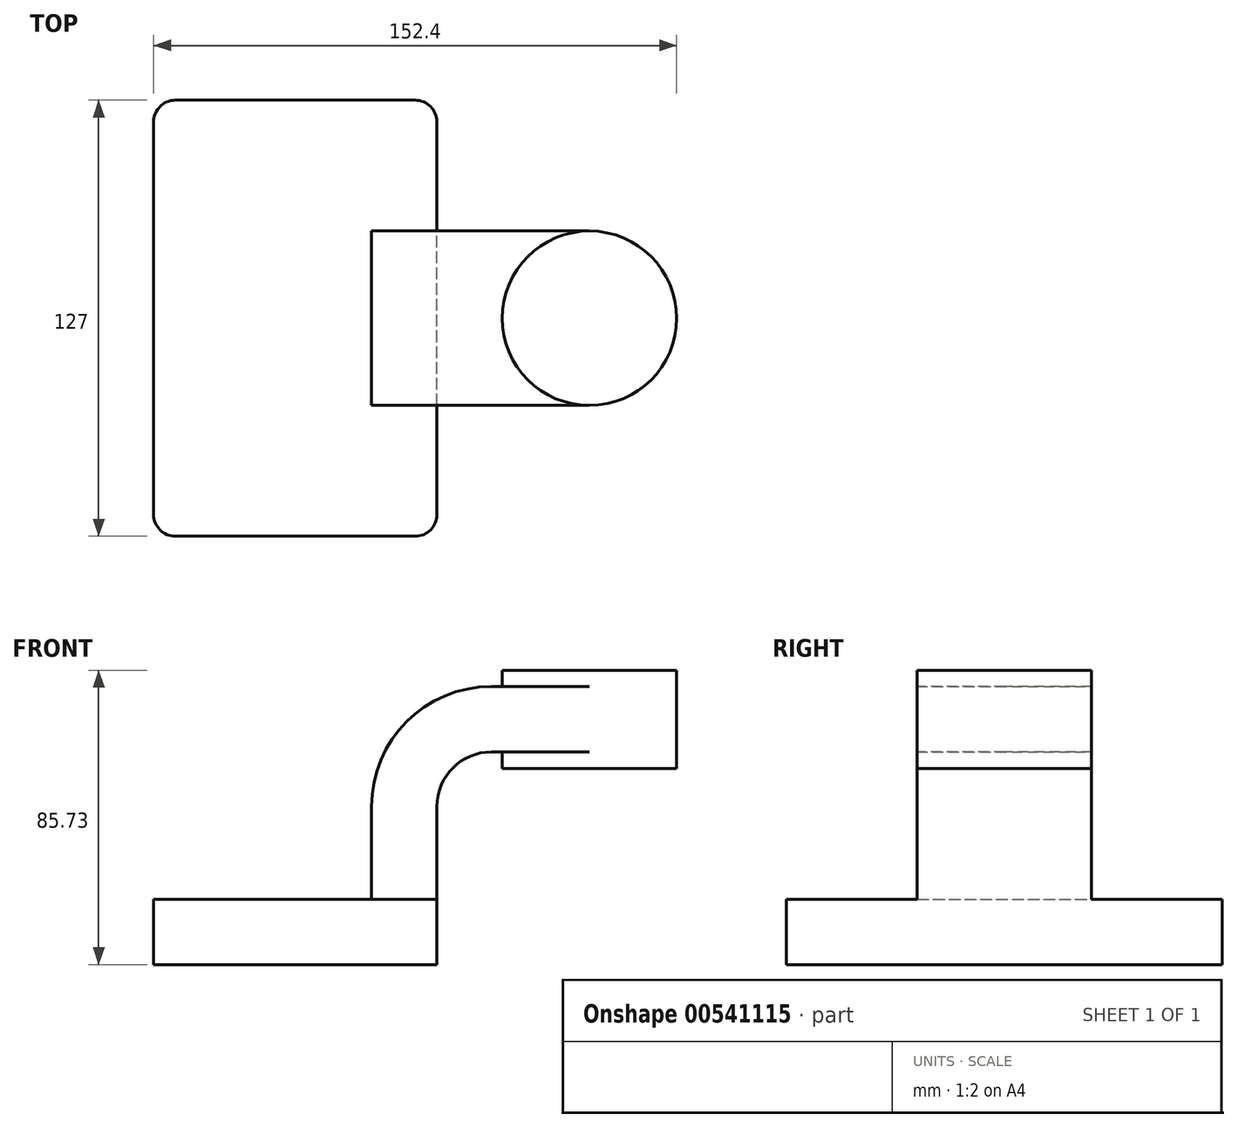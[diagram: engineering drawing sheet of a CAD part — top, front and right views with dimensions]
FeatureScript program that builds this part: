
annotation { "Feature Type Name" : "Feature", "Feature Type Description" : "" }
export const myFeature = defineFeature(function(context is Context, id is Id, definition is map)
    precondition{}
    {
        {
            var Q0;
            Q0=qCreatedBy(makeId("Front.planeOp"),FACE);
            var sketch = newSketch(context, id + "F0", { "sketchPlane" : qUnion([Q0])});
            skLineSegment(sketch, "E0.bottom", {"start": v(41.28, -9.52) * mm, "end": v(-41.27, -9.53) * mm});
            skLineSegment(sketch, "E0.top", {"start": v(41.27, 9.53) * mm, "end": v(-41.28, 9.53) * mm});
            skLineSegment(sketch, "E0.left", {"start": v(41.28, -9.52) * mm, "end": v(41.28, 9.53) * mm});
            skLineSegment(sketch, "E0.right", {"start": v(-41.27, -9.52) * mm, "end": v(-41.28, 9.53) * mm});
            skPoint(sketch, "E0.middle", {"position": v(0, 0) * mm});
            skLineSegment(sketch, "E1.bottom", {"start": v(111.12, 47.63) * mm, "end": v(60.33, 47.62) * mm});
            skLineSegment(sketch, "E1.top", {"start": v(111.12, 76.2) * mm, "end": v(60.33, 76.2) * mm});
            skLineSegment(sketch, "E1.left", {"start": v(111.12, 47.62) * mm, "end": v(111.12, 76.2) * mm});
            skLineSegment(sketch, "E1.right", {"start": v(60.33, 47.62) * mm, "end": v(60.33, 76.2) * mm});
            skPoint(sketch, "E1.middle", {"position": v(85.72, 61.91) * mm});
            skLineSegment(sketch, "E2", {"start": v(41.27, 9.53) * mm, "end": v(41.27, 36.53) * mm});
            skArc(sketch, "E3", {"start": v(41.27, 36.53) * mm, "mid": v(45.92, 47.75) * mm, "end": v(57.15, 52.4) * mm});
            skLineSegment(sketch, "E4", {"start": v(57.15, 52.4) * mm, "end": v(85.72, 52.4) * mm});
            skLineSegment(sketch, "E5.0", {"start": v(57.15, 71.45) * mm, "end": v(85.72, 71.45) * mm});
            skArc(sketch, "E5.1", {"start": v(22.23, 36.53) * mm, "mid": v(32.45, 61.22) * mm, "end": v(57.15, 71.45) * mm});
            skLineSegment(sketch, "E5.2", {"start": v(22.22, 9.53) * mm, "end": v(22.22, 36.53) * mm});
            skLineSegment(sketch, "E6", {"start": v(85.72, 47.62) * mm, "end": v(85.72, 76.2) * mm});
            skFitSpline(sketch, "E7", {"points": [v(-41.28, 9.53) * mm, v(57.15, 71.45) * mm], "startDerivative": vector(106.2, 48.35) * mm, "endDerivative": vector(171.45, -4.72) * mm});
            skSolve(sketch);
        }
        {
            var Q0;
            Q0=makeQuery(id+"F0.imprint","IMPRINT",FACE,{"disambiguationData":[TD([[makeQuery(id+"F0.imprint","IMPRINT",EDGE,{"derivedFrom":sQuery(id+"F0.wireOp",EDGE,"E0.bottom")}),-1.0]])]});
            extrude(context, id + "F1", {"entities" : qUnion([Q0]), "depth" : 127 * mm, "offsetDistance" : 25.4 * mm, "symmetric" : true});
        }
        {
            var Q0;
            {var subQ1=sQuery(id+"F0.wireOp",EDGE,"E2");Q0=makeQuery(id+"F0.imprint","IMPRINT",FACE,{"disambiguationData":[TD([[makeQuery(id+"F0.imprint","IMPRINT",EDGE,{"derivedFrom":subQ1}),1.0]])]});}
            var Q1;
            {var subQ0=sQuery(id+"F0.wireOp",EDGE,"E4");var subQ1=sQuery(id+"F0.wireOp",EDGE,"E1.right");var subQ2=makeQuery(id+"F0.imprint","INTERSECT",VERTEX,{"derivedFrom":[subQ1,subQ0]});Q1=makeQuery(id+"F0.imprint","IMPRINT",FACE,{"disambiguationData":[TD([[makeQuery(id+"F0.imprint","IMPRINT",EDGE,{"disambiguationData":[TD([[subQ2,-1.0]])],"derivedFrom":subQ1}),-1.0]])]});}
            extrude(context, id + "F2", {"entities" : qUnion([Q0, Q1]), "operationType" : NewBodyOperationType.ADD, "depth" : 50.8 * mm, "offsetDistance" : 25.4 * mm, "symmetric" : true});
        }
        {
            var Q0;
            Q0=makeQuery(id+"F0.imprint","IMPRINT",FACE,{"disambiguationData":[TD([[makeQuery(id+"F0.imprint","IMPRINT",EDGE,{"derivedFrom":sQuery(id+"F0.wireOp",EDGE,"E5.1")}),1.0]])]});
            extrude(context, id + "F3", {"entities" : qUnion([Q0]), "operationType" : NewBodyOperationType.ADD, "depth" : 15.88 * mm, "offsetDistance" : 25.4 * mm, "symmetric" : true});
        }
        {
            var Q0;
            {var subQ4=sQuery(id+"F0.wireOp",EDGE,"E1.left");Q0=makeQuery(id+"F0.imprint","IMPRINT",FACE,{"disambiguationData":[TD([[makeQuery(id+"F0.imprint","IMPRINT",EDGE,{"derivedFrom":subQ4}),1.0]])]});}
            var Q1;
            Q1=sQuery(id+"F0.wireOp",EDGE,"E6");
            revolve(context, id + "F4", {"operationType" : NewBodyOperationType.ADD, "entities" : qUnion([Q0]), "axis" : qUnion([Q1]), "revolveType" : RevolveType.FULL});
        }
        {
            var Q0;
            Q0=makeQuery(id+"F1.opExtrude","CAP_EDGE",EDGE,{"disambiguationData":[OSD([sQuery(id+"F0.wireOp",EDGE,"E0.right")])],"isStart":false});
            var Q1;
            Q1=makeQuery(id+"F1.opExtrude","CAP_EDGE",EDGE,{"disambiguationData":[OSD([sQuery(id+"F0.wireOp",EDGE,"E0.left")])],"isStart":false});
            var Q2;
            Q2=makeQuery(id+"F1.opExtrude","CAP_EDGE",EDGE,{"disambiguationData":[OSD([sQuery(id+"F0.wireOp",EDGE,"E0.left")])],"isStart":true});
            var Q3;
            Q3=makeQuery(id+"F1.opExtrude","CAP_EDGE",EDGE,{"disambiguationData":[OSD([sQuery(id+"F0.wireOp",EDGE,"E0.right")])],"isStart":true});
            fillet(context, id + "F5", {"entities" : qUnion([Q0, Q1, Q2, Q3]), "radius" : 6.35 * mm, "tangentPropagation" : true, "allowEdgeOverflow" : false});
        }
    });
